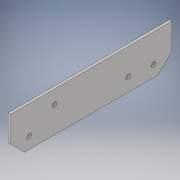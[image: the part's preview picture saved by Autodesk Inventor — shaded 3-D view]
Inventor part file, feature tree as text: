
AUTODESK INVENTOR PART (.ipt)
format: ipt  version: 2017 (Build 210142000, 142)  size: 120,832 bytes
history: native  units: in
note: dims shown in document units (in); Inventor stores cm internally (conversion verified against a paired STEP export)
features: extrude x2, chamfer x2, sketch x2, projected_geometry x1
ambient origin geometry x8: Origin, YZ Plane, XZ Plane, XY Plane, X Axis, Y Axis, Z Axis, Center Point
bodies: Solid1 (feature_tree)
feature tree (7):
  extrude  "Extrusion1"  Depth=17.5in
  chamfer  "Chamfer1"  Distance=1.25in
  chamfer  "Chamfer2"  Distance=2.0in
  extrude  "Extrusion2"  Depth=0.25in
  sketch  "Sketch1"  dims[d0=4.326in d1=17.5in]
  sketch  "Sketch2"  dims[d2=0.501in d3=1.25in d4=2.0in d5=2.0in d6=0.25in d7=0.0in d8=1.5in d9=0.125in d10=45.0deg d11=1.5in d12=0.125in d13=45.0deg d14=0.501in d15=4.741in d16=1.469in d17=0.501in d18=1.469in d19=4.741in d20=1.0in d21=0.0in]
  projected_geometry  "Projected Loop1"
